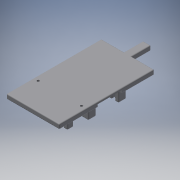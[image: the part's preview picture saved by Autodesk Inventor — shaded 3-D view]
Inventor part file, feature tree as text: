
AUTODESK INVENTOR PART (.ipt)
format: ipt  version: 2018 (Build 220112000, 112)  size: 1,128,448 bytes
history: native  units: mm
features: projected_geometry x64, reference x34, extrude x22, sketch x21, fillet x14, other x12, plane x4
ambient origin geometry x8: Origin, YZ Plane, XZ Plane, XY Plane, X Axis, Y Axis, Z Axis, Center Point
bodies: Solid1 (feature_tree)
feature tree (171):
  extrude  "Extrusion1"  Depth=40.0mm
  sketch  "Sketch3"  dims[d4=110.0mm d5=130.0mm]
  extrude  "Extrusion3"  Depth=130.0mm
  extrude  "Extrusion4"  Depth=20.0mm
  extrude  "Extrusion5"  Depth=10.0mm TaperAngle=0.0deg
  extrude  "Extrusion7"  Depth=25.0mm TaperAngle=0.0deg
  extrude  "Extrusion8"  Depth=5.0mm TaperAngle=0.0deg
  extrude  "Extrusion9"  Depth=20.0mm TaperAngle=0.0deg
  fillet  "Fillet1"  Radius=25.0mm
  extrude  "Extrusion10"  Depth=160.0mm TaperAngle=0.0deg
  extrude  "Extrusion11"  Depth=40.0mm TaperAngle=0.0deg
  extrude  "Extrusion12"  Depth=1.0mm TaperAngle=0.0deg
  sketch  "Sketch16"  dims[d77=1.0mm d78=60.0mm d79=0.0mm]
  plane  "Work Plane2"
  extrude  "Extrusion13"  Depth=4.572mm
  fillet  "Fillet2"  Radius=10.0mm
  fillet  "Fillet3"  Radius=0.2mm
  fillet  "Fillet4"  Radius=4.118mm
  fillet  "Fillet5"  Radius=4.572mm
  extrude  "Extrusion14"  Depth=16.002mm
  fillet  "Fillet6"  Radius=8.0mm
  plane  "Work Plane3"
  extrude  "Extrusion15"  Depth=1.0mm
  extrude  "Extrusion16"  Depth=1.0mm
  sketch  "Sketch20"  dims[d90=10.0mm d91=0.0mm d92=1.0mm]
  plane  "Work Plane4"
  extrude  "Extrusion17"  Depth=1.0mm
  sketch  "Sketch21"  dims[d93=1.0mm d94=1.0mm]
  plane  "Work Plane5"
  extrude  "Extrusion18"  Depth=10.0mm TaperAngle=0.0deg
  fillet  "Fillet9"  Radius=1.0mm
  fillet  "Fillet10"  Radius=10.0mm
  fillet  "Fillet11"  Radius=5.0mm
  fillet  "Fillet12"  Radius=5.0mm
  fillet  "Fillet13"  Radius=2.5mm
  extrude  "Extrusion21"  Depth=10.0mm
  fillet  "Fillet16"  Radius=10.0mm
  extrude  "Extrusion22"  Depth=20.0mm
  extrude  "Extrusion23"  Depth=2.0mm
  extrude  "Extrusion24"  Depth=1.0mm
  extrude  "Extrusion25"  Depth=2.4mm
  extrude  "Extrusion26"  Depth=2.0mm
  fillet  "Fillet19"  Radius=2.0mm
  fillet  "Fillet20"  Radius=4.0mm
  sketch  "Sketch1"  dims[d2=40.0mm d3=40.0mm]
  reference  "Reference1"
  reference  "Reference2"
  sketch  "Sketch6"  dims[d6=130.0mm d7=20.0mm]
  sketch  "Sketch8"  dims[d8=20.0mm d9=10.0mm d10=0.0mm]
  sketch  "Sketch10"  dims[d17=40.0mm d25=25.0mm d26=0.0mm]
  sketch  "Sketch11"  dims[d27=160.0mm d28=0.0mm]
  sketch  "Sketch12"  dims[d53=36.0mm d54=36.0mm d55=99.0mm d56=117.0mm d57=117.0mm d58=18.0mm d59=18.0mm d60=160.0mm d61=5.0mm d62=0.0mm d63=0.0mm]
  reference  "Reference3"
  reference  "Reference4"
  reference  "Reference5"
  reference  "Reference6"
  reference  "Reference7"
  projected_geometry  "Projected Loop5"
  projected_geometry  "Projected Loop6"
  sketch  "Sketch13"  dims[d66=20.0mm d67=12.5mm d68=0.0mm d69=25.0mm]
  projected_geometry  "Projected Loop7"
  sketch  "Sketch14"  dims[d70=160.0mm d71=0.0mm d72=160.0mm d73=0.0mm]
  reference  "Reference8"
  sketch  "Sketch15"  dims[d74=6.0mm d75=40.0mm d76=0.0mm]
  reference  "Reference9"
  reference  "Reference10"
  reference  "Reference11"
  reference  "Reference12"
  reference  "Reference13"
  reference  "Reference14"
  reference  "Reference15"
  projected_geometry  "Projected Loop8"
  reference  "Reference16"
  reference  "Reference17"
  reference  "Reference18"
  reference  "Reference19"
  reference  "Reference20"
  reference  "Reference21"
  reference  "Reference22"
  reference  "Reference23"
  reference  "Reference24"
  reference  "Reference25"
  reference  "Reference26"
  reference  "Reference27"
  sketch  "Sketch17"  dims[d80=1.0mm d81=8.35mm d82=10.0mm d83=0.0mm d84=0.2mm d85=4.118mm d86=4.572mm]
  reference  "Reference28"
  reference  "Reference29"
  reference  "Reference30"
  projected_geometry  "Projected Loop9"
  projected_geometry  "Projected Loop10"
  projected_geometry  "Projected Loop11"
  projected_geometry  "Projected Loop12"
  projected_geometry  "Projected Loop13"
  projected_geometry  "Projected Loop14"
  projected_geometry  "Projected Loop15"
  projected_geometry  "Projected Loop16"
  projected_geometry  "Projected Loop17"
  projected_geometry  "Projected Loop18"
  projected_geometry  "Projected Loop19"
  projected_geometry  "Projected Loop20"
  projected_geometry  "Projected Loop21"
  projected_geometry  "Projected Loop22"
  projected_geometry  "Projected Loop23"
  projected_geometry  "Projected Loop24"
  projected_geometry  "Projected Loop25"
  projected_geometry  "Projected Loop26"
  projected_geometry  "Projected Loop27"
  projected_geometry  "Projected Loop28"
  projected_geometry  "Projected Loop29"
  projected_geometry  "Projected Loop30"
  projected_geometry  "Projected Loop31"
  projected_geometry  "Projected Loop32"
  projected_geometry  "Projected Loop33"
  projected_geometry  "Projected Loop34"
  projected_geometry  "Projected Loop35"
  projected_geometry  "Projected Loop36"
  projected_geometry  "Projected Loop37"
  projected_geometry  "Projected Loop38"
  projected_geometry  "Projected Loop39"
  projected_geometry  "Projected Loop40"
  projected_geometry  "Projected Loop41"
  projected_geometry  "Projected Loop42"
  projected_geometry  "Projected Loop43"
  projected_geometry  "Projected Loop44"
  projected_geometry  "Projected Loop45"
  projected_geometry  "Projected Loop46"
  projected_geometry  "Projected Loop47"
  projected_geometry  "Projected Loop48"
  projected_geometry  "Projected Loop49"
  projected_geometry  "Projected Loop50"
  projected_geometry  "Projected Loop51"
  projected_geometry  "Projected Loop52"
  projected_geometry  "Projected Loop53"
  projected_geometry  "Projected Loop54"
  projected_geometry  "Projected Loop55"
  projected_geometry  "Projected Loop56"
  projected_geometry  "Projected Loop57"
  projected_geometry  "Projected Loop58"
  projected_geometry  "Projected Loop59"
  projected_geometry  "Projected Loop60"
  projected_geometry  "Projected Loop61"
  projected_geometry  "Projected Loop62"
  sketch  "Sketch19"  dims[d87=2.94mm d88=16.002mm d89=8.0mm]
  reference  "Reference31"
  projected_geometry  "Projected Loop63"
  projected_geometry  "Projected Loop64"
  projected_geometry  "Projected Loop65"
  projected_geometry  "Projected Loop66"
  sketch  "Sketch24"  dims[d95=1.0mm d96=1.0mm]
  reference  "Reference34"
  sketch  "Sketch25"  dims[d97=1.0mm d98=10.0mm d99=0.0mm d100=1.0mm d101=10.0mm d102=0.0mm d103=5.0mm d104=5.0mm d105=2.5mm]
  reference  "Reference35"
  sketch  "Sketch26"  dims[d106=18.0mm d107=2.5mm d108=10.0mm d109=0.0mm]
  sketch  "Sketch27"  dims[d110=20.0mm d111=9.75mm]
  sketch  "Sketch28"  dims[d112=19.5mm d113=2.0mm]
  projected_geometry  "Projected Loop67"
  reference  "Reference36"
  sketch  "Sketch29"  dims[d114=0.2mm d115=0.2mm d116=2.4mm d117=2.0mm d118=2.0mm d119=4.0mm d120=2.0mm d121=4.0mm d122=10.0mm d123=0.0mm d124=25.5mm d125=10.0mm d126=0.0mm d129=1.0mm d130=1.0mm d131=1.0mm d132=1.0mm d133=0.5mm d153=10.0mm d154=0.0mm d155=1.0mm d156=2.75mm d157=10.0mm d158=0.0mm d159=70.0mm d160=25.0mm d161=10.0mm d162=0.0mm d164=30.0mm d165=4.0mm d166=8.0mm d167=20.0mm d168=100.0mm d169=0.0mm d171=10.0mm d172=0.0mm d173=10.0mm d174=0.0mm d175=1.0mm d176=1.0mm]
  projected_geometry  "Projected Loop68"
  other  "<userpath>\OneDrive\Documents\Inventor\TSA\2018\Animatronics\Tortoise\Head\HeadAssembly.iam"
  other  "HeadAssembly.iam"
  other  "HeadBase:1"
  other  "Rack:2"
  other  "Rack:1"
  other  "HeadTop:1"
  other  "<userpath>\OneDrive\Documents\Inventor\TSA\2018\Animatronics\Tortoise\TurtleAssembly.iam"
  other  "TurtleAssembly.iam"
  other  "servo (2):4"
  other  "servo (2):5"
  other  "SyringeConnector:1"
  other  "FlexHinge:1"
